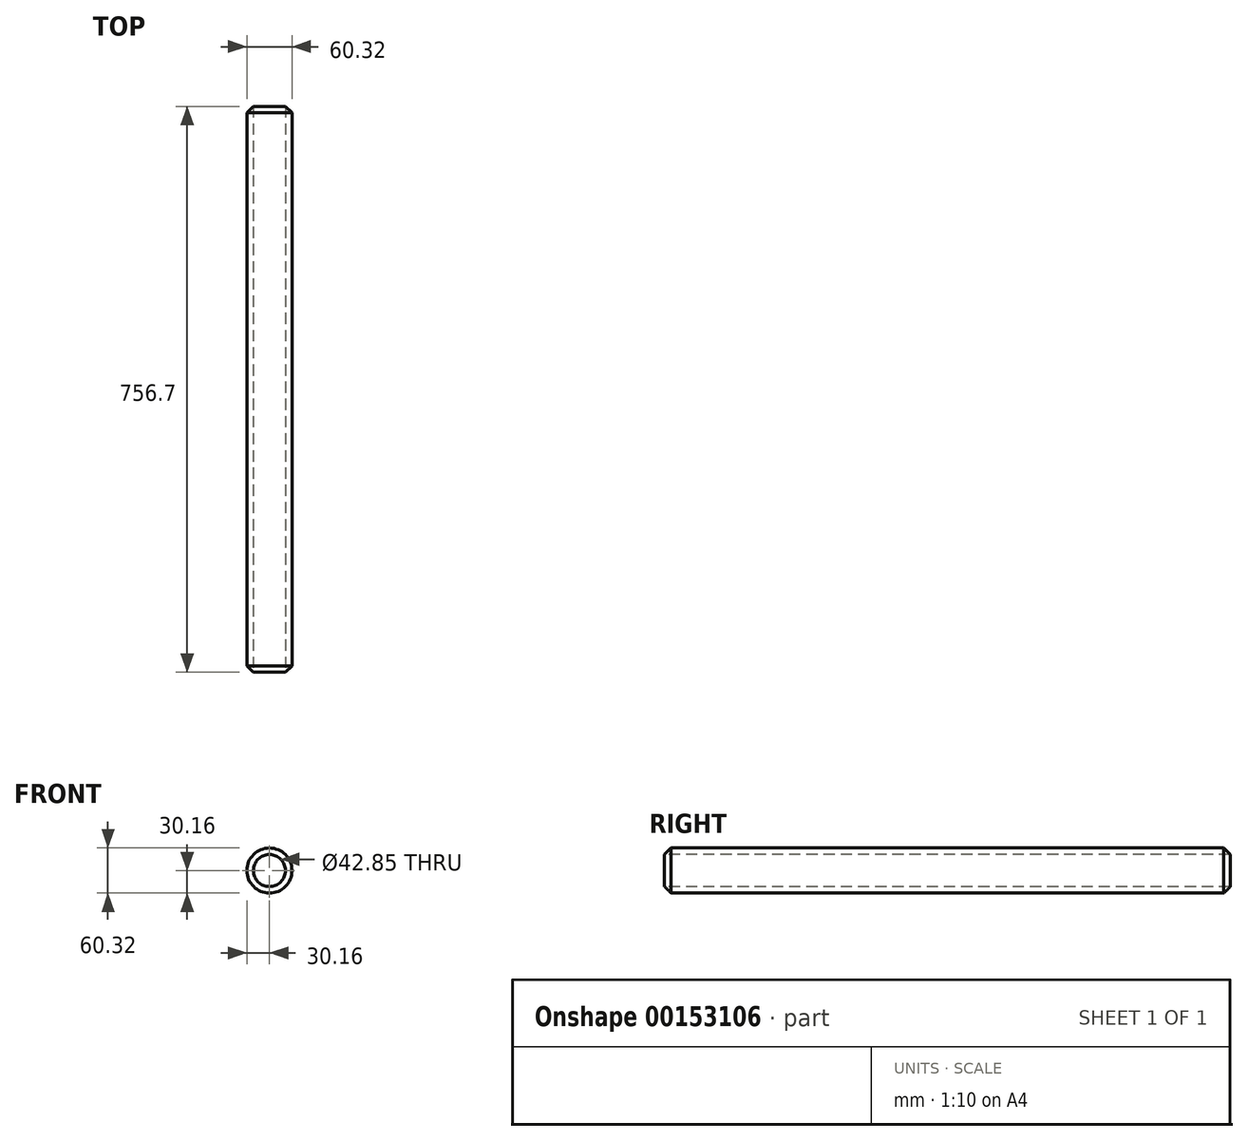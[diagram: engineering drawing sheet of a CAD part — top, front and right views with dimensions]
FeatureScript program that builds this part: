
annotation { "Feature Type Name" : "Feature", "Feature Type Description" : "" }
export const myFeature = defineFeature(function(context is Context, id is Id, definition is map)
    precondition{}
    {
        {
            var Q0;
            Q0=qCreatedBy(makeId("Front.planeOp"),FACE);
            var sketch = newSketch(context, id + "F0", { "sketchPlane" : qUnion([Q0])});
            skCircle(sketch, "E0", {"center": v(0, 0) * mm, "radius": 30.16 * mm});
            skSolve(sketch);
        }
        {
            var Q0;
            Q0=makeQuery(id+"F0.imprint","IMPRINT",FACE,{"disambiguationData":[TD([[makeQuery(id+"F0.imprint","IMPRINT",EDGE,{"derivedFrom":sQuery(id+"F0.wireOp",EDGE,"E0")}),1.0]])]});
            extrude(context, id + "F1", {"entities" : qUnion([Q0]), "depth" : 762 * mm});
        }
        {
            var Q0;
            Q0=makeQuery(id+"F1.opExtrude","CAP_FACE",FACE,{"disambiguationData":[OSD([sQuery(id+"F0.wireOp",EDGE,"E0")])],"isStart":false});
            var sketch = newSketch(context, id + "F2", { "sketchPlane" : qUnion([Q0])});
            skPoint(sketch, "E1", {"position": v(0, 0) * mm});
            skSolve(sketch);
        }
        {
            var Q0;
            Q0=sQuery(id+"F2.wireOp",VERTEX,"E1");
            var Q1;
            Q1=makeQuery(id+"F1.opExtrude","SWEPT_BODY",BODY,{"disambiguationData":[OSD([sQuery(id+"F0.wireOp",EDGE,"E0")])]});
            hole(context, id + "F3", {"style" : HoleStyle.SIMPLE, "endStyle" : HoleEndStyle.THROUGH, "holeDiameter" : 42.85 * mm, "locations" : qUnion([Q0]), "scope" : qUnion([Q1]), "isTappedThrough" : true});
        }
        {
            var Q0;
            Q0=makeQuery(id+"F1.opExtrude","CAP_EDGE",EDGE,{"disambiguationData":[OSD([sQuery(id+"F0.wireOp",EDGE,"E0")])],"isStart":false});
            var Q1;
            Q1=makeQuery(id+"F1.opExtrude","CAP_EDGE",EDGE,{"disambiguationData":[OSD([sQuery(id+"F0.wireOp",EDGE,"E0")])],"isStart":true});
            chamfer(context, id + "F4", {"entities" : qUnion([Q0, Q1]), "width" : 11.4 * mm, "tangentPropagation" : true});
        }
    });
